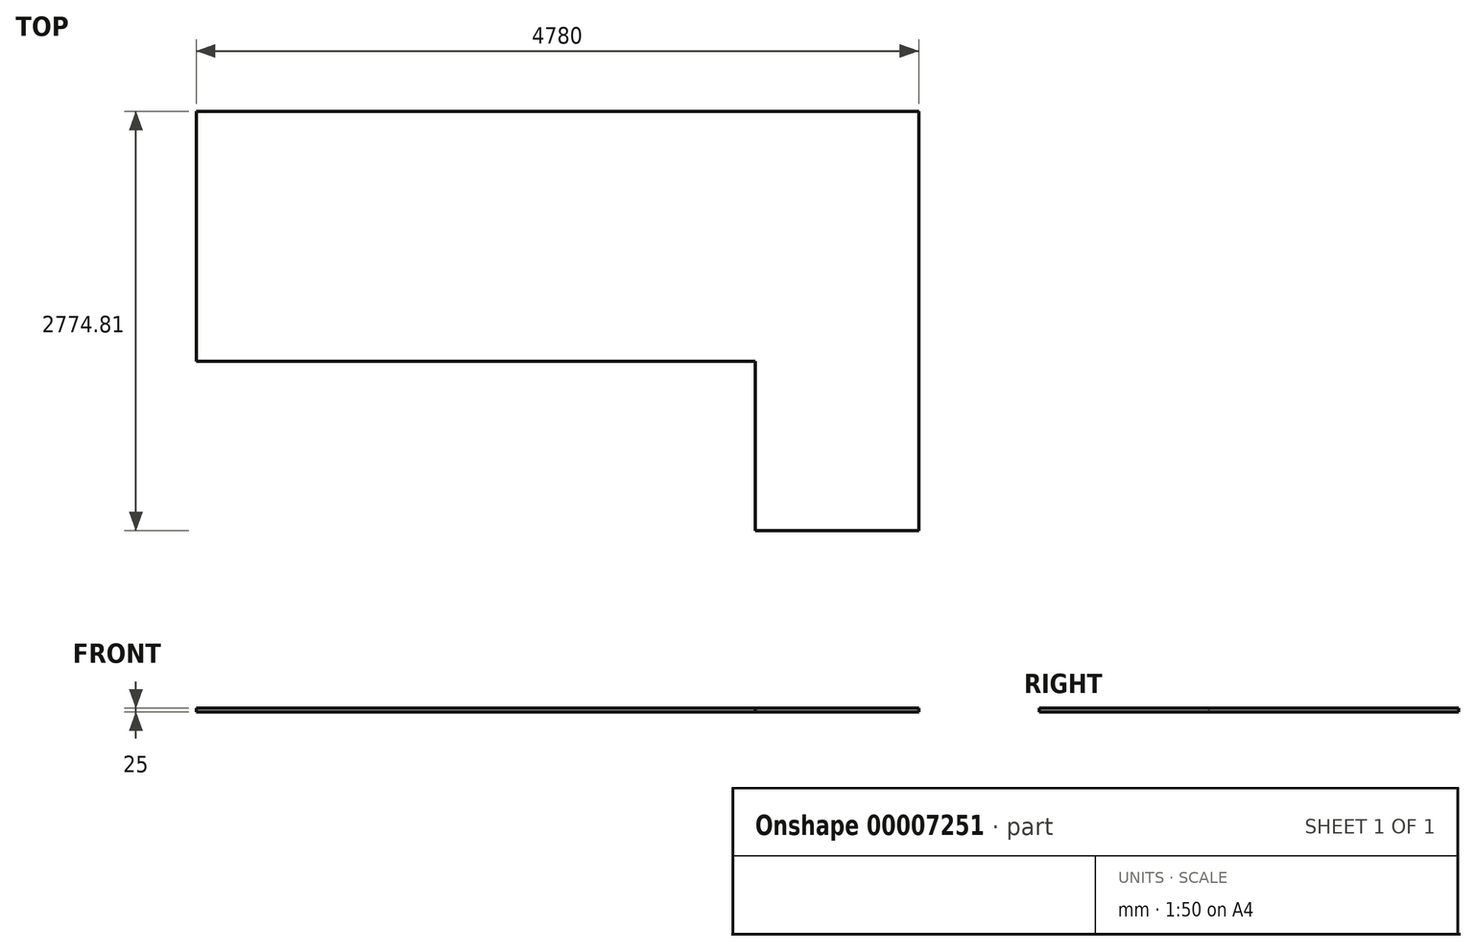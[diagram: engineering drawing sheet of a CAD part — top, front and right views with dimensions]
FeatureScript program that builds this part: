
annotation { "Feature Type Name" : "Feature", "Feature Type Description" : "" }
export const myFeature = defineFeature(function(context is Context, id is Id, definition is map)
    precondition{}
    {
        {
            var Q0;
            Q0=qCreatedBy(makeId("Top.planeOp"),FACE);
            var sketch = newSketch(context, id + "F0", { "sketchPlane" : qUnion([Q0])});
            skLineSegment(sketch, "E0.0", {"start": v(4942.46, 1586.53) * mm, "end": v(4942.46, -1188.28) * mm});
            skLineSegment(sketch, "E0.1", {"start": v(162.46, 1586.53) * mm, "end": v(4942.46, 1586.53) * mm});
            skLineSegment(sketch, "E0.2", {"start": v(162.46, -68.47) * mm, "end": v(162.46, 1586.53) * mm});
            skLineSegment(sketch, "E0.3", {"start": v(3862.46, -68.47) * mm, "end": v(162.46, -68.47) * mm});
            skLineSegment(sketch, "E0.4", {"start": v(3862.46, -1188.28) * mm, "end": v(3862.46, -68.47) * mm});
            skLineSegment(sketch, "E1", {"start": v(3862.46, -1188.28) * mm, "end": v(4942.46, -1188.28) * mm});
            skSolve(sketch);
        }
        {
            var Q0;
            Q0=makeQuery(id+"F0.imprint","IMPRINT",FACE,{"disambiguationData":[TD([[makeQuery(id+"F0.imprint","IMPRINT",EDGE,{"derivedFrom":sQuery(id+"F0.wireOp",EDGE,"E0.0")}),-1.0]])]});
            extrude(context, id + "F1", {"entities" : qUnion([Q0]), "depth" : 25 * mm});
        }
    });
